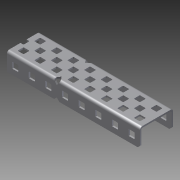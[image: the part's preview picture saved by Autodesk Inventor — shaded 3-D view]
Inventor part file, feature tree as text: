
AUTODESK INVENTOR PART (.ipt)
format: ipt  version: 2014 SP1 (Build 180222100, 222)  size: 727,040 bytes
history: native  units: in
note: dims shown in document units (in); Inventor stores cm internally (conversion verified against a paired STEP export)
features: other x1, imported_body x1, extrude x1, sketch x1
ambient origin geometry x8: Origin, YZ Plane, XZ Plane, XY Plane, X Axis, Y Axis, Z Axis, Center Point
bodies: Body1 (feature_tree)
feature tree (4):
  parser-record x1  (decoder bookkeeping rows leaked as tree rows — omitted from the tree; the rows remain in map.json)
  imported_body  "Base1"
  extrude  "Extrusion1"  Depth=1.0in TaperAngle=0.0deg
  sketch  "Sketch2"  dims[d0=1.0in d1=1.0in d2=0.0in]
